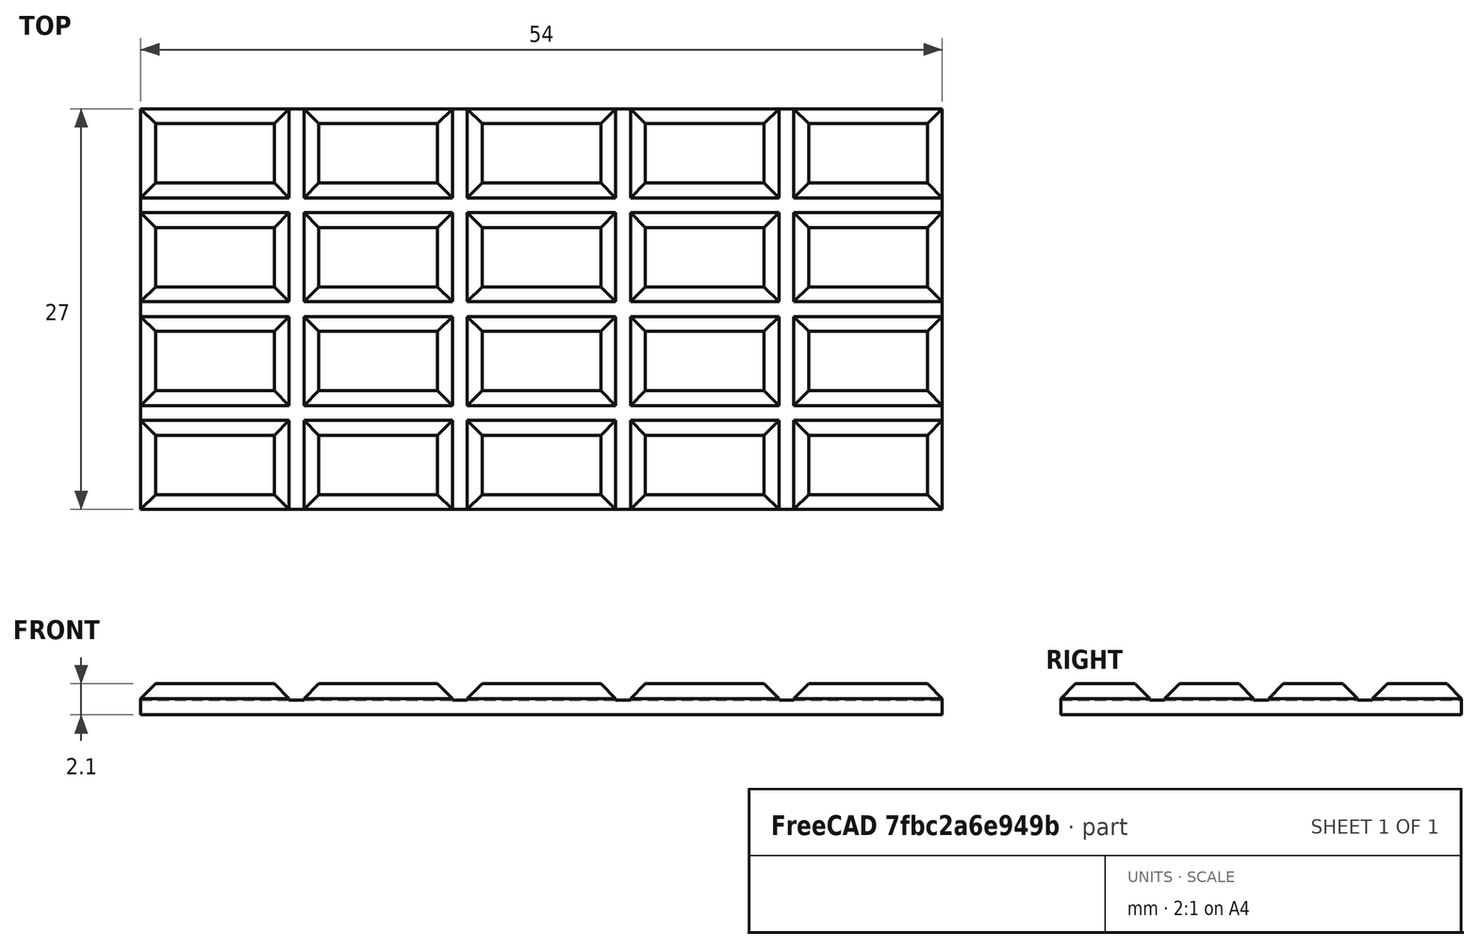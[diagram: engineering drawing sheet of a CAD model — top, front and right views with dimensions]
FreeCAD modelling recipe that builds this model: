
FCSTD DOCUMENT  (FreeCAD 0.18.4R)
Label: tutorial_freecad_ex12_c
License: All rights reserved
LicenseURL: http://en.wikipedia.org/wiki/All_rights_reserved
objects: Part::Box×2, Part::Chamfer×1, Part::FeaturePython×1, Part::MultiFuse×1
note: 5 computed .brp shape members not serialized (recipe doc carries the construction recipe); baked Part::Feature solids carry a one-line shape summary decoded from their .brp

FEATURE [Part::Box] Box  label="base"
  AttacherType = Attacher::AttachEngine3D
  Height = 1
  Length = 54
  Width = 27
FEATURE [Part::Box] Box001  label="onza"
  AttacherType = Attacher::AttachEngine3D
  Height = 1.1
  Length = 10
  Placement = pos=(0,0,1) rot=(0,0,1;0rad)
  Width = 6
FEATURE [Part::Chamfer] Chamfer
  Base = -> Box001
  Edges = 4 edges r=1: [Edge2,Edge6,Edge10,Edge12]
FEATURE [Part::FeaturePython] Array  label="array_onzas"  # Draft array (typed FeaturePython)
  Angle = 360
  ArrayType = 0
  Axis = (0,0,1)
  Base = -> Chamfer
  Center = (0,0,0)
  Fuse = false
  IntervalAxis = (0,0,0)
  IntervalX = (11,0,0)
  IntervalY = (0,7,0)
  IntervalZ = (0,0,1)
  NumberPolar = 1
  NumberX = 5
  NumberY = 4
  NumberZ = 1
FEATURE [Part::MultiFuse] Fusion  label="tableta"
  Refine = true
  Shapes = -> [Box,Array]
